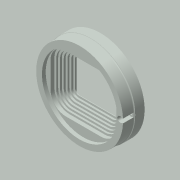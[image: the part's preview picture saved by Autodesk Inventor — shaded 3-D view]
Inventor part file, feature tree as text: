
AUTODESK INVENTOR PART (.ipt)
format: ipt  version: 2015 (Build 190159000, 159)  size: 452,608 bytes
history: native  units: in
note: dims shown in document units (in); Inventor stores cm internally (conversion verified against a paired STEP export)
features: extrude x17, sketch x17, reference x4, fillet x1
ambient origin geometry x8: Origin, YZ Plane, XZ Plane, XY Plane, X Axis, Y Axis, Z Axis, Center Point
bodies: Solid1 (feature_tree)
feature tree (39):
  extrude  "Extrusion1"  Depth=0.3937in TaperAngle=0.0deg
  extrude  "Extrusion14"  Depth=0.315in TaperAngle=0.0deg
  extrude  "Extrusion15"  Depth=0.6339in
  extrude  "Extrusion39"  Depth=0.0394in
  extrude  "Extrusion17"  Depth=0.315in TaperAngle=0.0deg
  extrude  "Extrusion18"  Depth=0.2756in TaperAngle=0.0deg
  extrude  "Extrusion19"  Depth=0.2362in TaperAngle=0.0deg
  extrude  "Extrusion20"  Depth=0.1969in TaperAngle=0.0deg
  extrude  "Extrusion21"  Depth=0.1575in TaperAngle=0.0deg
  extrude  "Extrusion22"  Depth=0.1181in TaperAngle=0.0deg
  extrude  "Extrusion23"  Depth=0.0787in TaperAngle=0.0deg
  extrude  "Extrusion24"  Depth=0.0394in TaperAngle=0.0deg
  extrude  "Extrusion25"  Depth=0.9843in
  extrude  "Extrusion38"  Depth=0.1102in
  sketch  "Sketch40"  dims[d137=0.0394in d138=0.0394in d139=0.0in]
  extrude  "Extrusion40"  Depth=2.3622in
  extrude  "Extrusion41"  Depth=0.0197in
  extrude  "Extrusion42"  Depth=0.0197in
  fillet  "Fillet1"  Radius=0.1575in
  sketch  "Sketch1"  dims[d9=0.1969in d10=0.0in]
  reference  "Reference2"
  reference  "Reference3"
  reference  "Reference4"
  reference  "Reference5"
  sketch  "Sketch15"  dims[d11=0.1181in d12=0.1181in d35=0.3937in d36=0.5906in d37=0.7874in d38=0.9843in d39=0.3937in d40=0.5906in d41=1.1811in d42=1.378in d43=1.5748in d44=1.7717in d94=0.1969in d95=0.0in]
  sketch  "Sketch17"  dims[d96=1.811in d100=0.315in d101=0.0in]
  sketch  "Sketch18"  dims[d111=0.8189in d112=0.6339in]
  sketch  "Sketch19"  dims[d113=0.3543in d114=0.0in d115=0.0394in]
  sketch  "Sketch20"  dims[d116=0.0394in d117=0.315in d118=0.0in]
  sketch  "Sketch21"  dims[d119=0.0394in d120=0.2756in d121=0.0in]
  sketch  "Sketch22"  dims[d122=0.0394in d123=0.2362in d124=0.0in]
  sketch  "Sketch23"  dims[d125=0.0394in d126=0.1969in d127=0.0in]
  sketch  "Sketch24"  dims[d128=0.0394in d129=0.1575in d130=0.0in]
  sketch  "Sketch25"  dims[d131=0.0394in d132=0.1181in d133=0.0in]
  sketch  "Sketch39"  dims[d134=0.0394in d135=0.0787in d136=0.0in]
  sketch  "Sketch41"  dims[d217=0.9843in d219=0.9843in]
  sketch  "Sketch42"  dims[d220=0.063in d221=0.0in d222=0.1102in]
  sketch  "Sketch43"  dims[d223=0.2756in d231=2.3622in]
  sketch  "Sketch44"  dims[d233=1.5748in d234=1.1002in d264=2.2in d287=0.1575in d288=0.0787in d289=0.0in d291=1.5748in d292=1.5748in d293=0.1102in d294=0.1102in d295=1.0651in d296=1.0651in d297=2.2441in d298=1.2179in d299=0.9075in d300=1.0651in d301=0.1378in d302=1.0651in d303=0.9075in d304=0.1575in d305=0.1575in d306=1.5748in d307=1.815in d308=1.811in d310=1.9055in d311=0.0787in d312=0.0in d313=0.2992in d314=0.0in d315=0.1181in d317=0.8484in d318=0.1181in d319=0.0866in d320=0.1181in d321=0.0512in d323=0.1181in d324=0.0in d325=0.0197in d327=1.8504in]
